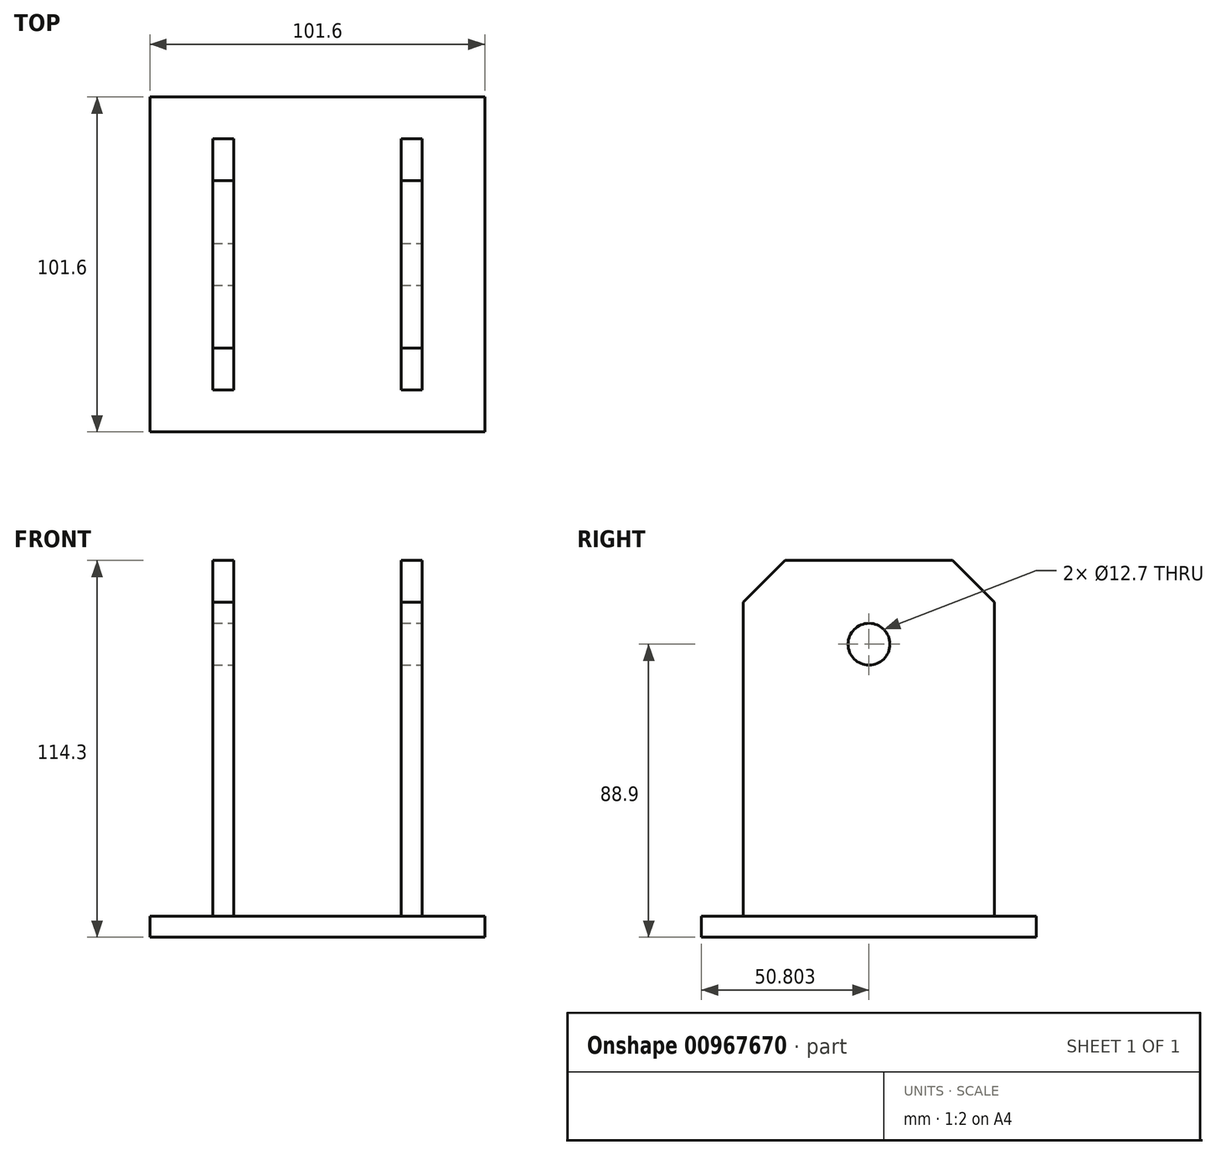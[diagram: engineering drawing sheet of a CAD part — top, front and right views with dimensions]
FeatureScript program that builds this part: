
annotation { "Feature Type Name" : "Feature", "Feature Type Description" : "" }
export const myFeature = defineFeature(function(context is Context, id is Id, definition is map)
    precondition{}
    {
        {
            var Q0;
            Q0=qCreatedBy(makeId("Top.planeOp"),FACE);
            var sketch = newSketch(context, id + "F0", { "sketchPlane" : qUnion([Q0])});
            skLineSegment(sketch, "E0.bottom", {"start": v(-72.56, -73.46) * mm, "end": v(29.04, -73.46) * mm});
            skLineSegment(sketch, "E0.top", {"start": v(-72.56, 28.14) * mm, "end": v(29.04, 28.14) * mm});
            skLineSegment(sketch, "E0.left", {"start": v(-72.56, -73.46) * mm, "end": v(-72.56, 28.14) * mm});
            skLineSegment(sketch, "E0.right", {"start": v(29.04, -73.46) * mm, "end": v(29.04, 28.14) * mm});
            skSolve(sketch);
        }
        {
            var Q0;
            Q0 = qSketchRegion(id + "F0", true);
            extrude(context, id + "F1", {"entities" : qUnion([Q0]), "depth" : 6.35 * mm, "offsetDistance" : 25.4 * mm});
        }
        {
            var Q0;
            Q0=makeQuery(id+"F1.opExtrude","CAP_FACE",FACE,{"disambiguationData":[OSD([sQuery(id+"F0.wireOp",EDGE,"E0.bottom"),sQuery(id+"F0.wireOp",EDGE,"E0.top"),sQuery(id+"F0.wireOp",EDGE,"E0.left"),sQuery(id+"F0.wireOp",EDGE,"E0.right")])],"isStart":false});
            var sketch = newSketch(context, id + "F2", { "sketchPlane" : qUnion([Q0])});
            skLineSegment(sketch, "E1.bottom", {"start": v(-53.51, -60.76) * mm, "end": v(-47.16, -60.76) * mm});
            skLineSegment(sketch, "E1.top", {"start": v(-53.51, 15.44) * mm, "end": v(-47.16, 15.44) * mm});
            skLineSegment(sketch, "E1.left", {"start": v(-53.51, -60.76) * mm, "end": v(-53.51, 15.44) * mm});
            skLineSegment(sketch, "E1.right", {"start": v(-47.16, -60.76) * mm, "end": v(-47.16, 15.44) * mm});
            skLineSegment(sketch, "E2.bottom", {"start": v(3.64, -60.76) * mm, "end": v(9.99, -60.76) * mm});
            skLineSegment(sketch, "E2.top", {"start": v(3.64, 15.44) * mm, "end": v(9.99, 15.44) * mm});
            skLineSegment(sketch, "E2.left", {"start": v(3.64, -60.76) * mm, "end": v(3.64, 15.44) * mm});
            skLineSegment(sketch, "E2.right", {"start": v(9.99, -60.76) * mm, "end": v(9.99, 15.44) * mm});
            skSolve(sketch);
        }
        {
            var Q0;
            Q0 = qSketchRegion(id + "F2", true);
            extrude(context, id + "F3", {"entities" : qUnion([Q0]), "operationType" : NewBodyOperationType.ADD, "depth" : 107.95 * mm, "offsetDistance" : 25.4 * mm});
        }
        {
            var Q0;
            Q0=makeQuery(id+"F3.opExtrude","SWEPT_FACE",FACE,{"disambiguationData":[OSD([sQuery(id+"F2.wireOp",EDGE,"E2.right")])]});
            var sketch = newSketch(context, id + "F4", { "sketchPlane" : qUnion([Q0])});
            skCircle(sketch, "E3", {"center": v(-22.66, 88.9) * mm, "radius": 6.35 * mm});
            skPoint(sketch, "E3.centerSnap0", {"position": v(-22.66, 114.3) * mm});
            skSolve(sketch);
        }
        {
            var Q0;
            Q0 = qSketchRegion(id + "F4", true);
            extrude(context, id + "F5", {"entities" : qUnion([Q0]), "operationType" : NewBodyOperationType.REMOVE, "endBound" : BoundingType.THROUGH_ALL, "oppositeDirection" : true, "depth" : 25.4 * mm, "offsetDistance" : 25.4 * mm});
        }
        {
            var Q0;
            Q0=makeQuery(id+"F3.opExtrude","CAP_EDGE",EDGE,{"disambiguationData":[OSD([sQuery(id+"F2.wireOp",EDGE,"E2.bottom")])],"isStart":false});
            var Q1;
            Q1=makeQuery(id+"F3.opExtrude","CAP_EDGE",EDGE,{"disambiguationData":[OSD([sQuery(id+"F2.wireOp",EDGE,"E2.top")])],"isStart":false});
            var Q2;
            Q2=makeQuery(id+"F3.opExtrude","CAP_EDGE",EDGE,{"disambiguationData":[OSD([sQuery(id+"F2.wireOp",EDGE,"E1.bottom")])],"isStart":false});
            var Q3;
            Q3=makeQuery(id+"F3.opExtrude","CAP_EDGE",EDGE,{"disambiguationData":[OSD([sQuery(id+"F2.wireOp",EDGE,"E1.top")])],"isStart":false});
            chamfer(context, id + "F6", {"entities" : qUnion([Q0, Q1, Q2, Q3]), "width" : 12.7 * mm, "tangentPropagation" : true});
        }
    });
